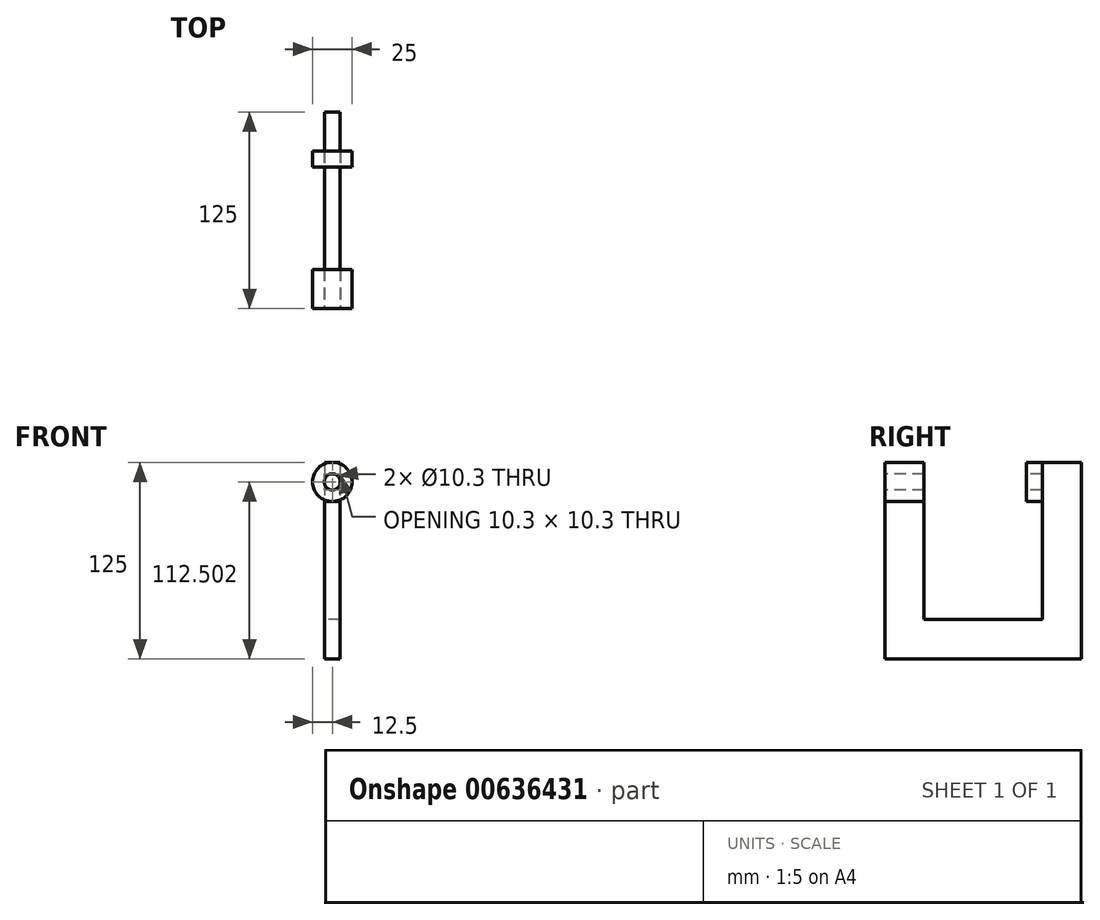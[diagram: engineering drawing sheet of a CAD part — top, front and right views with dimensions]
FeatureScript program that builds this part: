
annotation { "Feature Type Name" : "Feature", "Feature Type Description" : "" }
export const myFeature = defineFeature(function(context is Context, id is Id, definition is map)
    precondition{}
    {
        {
            var Q0;
            Q0=qCreatedBy(makeId("Right.planeOp"),FACE);
            var sketch = newSketch(context, id + "F0", { "sketchPlane" : qUnion([Q0])});
            skLineSegment(sketch, "E0", {"start": v(-109.86, 70.87) * mm, "end": v(-109.86, -29.13) * mm});
            skLineSegment(sketch, "E1", {"start": v(15.14, 95.87) * mm, "end": v(15.14, -29.13) * mm});
            skLineSegment(sketch, "E2", {"start": v(15.14, 95.87) * mm, "end": v(-9.86, 95.87) * mm});
            skLineSegment(sketch, "E3", {"start": v(-9.86, 95.87) * mm, "end": v(-9.86, -4.13) * mm});
            skLineSegment(sketch, "E4", {"start": v(-9.86, -4.13) * mm, "end": v(-84.86, -4.13) * mm});
            skLineSegment(sketch, "E5", {"start": v(-84.86, -4.13) * mm, "end": v(-84.86, 70.87) * mm});
            skLineSegment(sketch, "E6", {"start": v(-84.86, 70.87) * mm, "end": v(-109.86, 70.87) * mm});
            skLineSegment(sketch, "E7", {"start": v(-109.86, -29.13) * mm, "end": v(15.14, -29.13) * mm});
            skSolve(sketch);
        }
        {
            var Q0;
            Q0 = qSketchRegion(id + "F0", true);
            extrude(context, id + "F1", {"entities" : qUnion([Q0]), "endBound" : BoundingType.SYMMETRIC, "depth" : 10 * mm, "offsetDistance" : 25 * mm});
        }
        {
            var Q0;
            Q0=makeQuery(id+"F1.opExtrude","SWEPT_FACE",FACE,{"disambiguationData":[OSD([sQuery(id+"F0.wireOp",EDGE,"E3")])]});
            var sketch = newSketch(context, id + "F2", { "sketchPlane" : qUnion([Q0])});
            skCircle(sketch, "E8", {"center": v(0, 83.37) * mm, "radius": 12.5 * mm});
            skSolve(sketch);
        }
        {
            var Q0;
            Q0 = qSketchRegion(id + "F2", true);
            extrude(context, id + "F3", {"entities" : qUnion([Q0]), "depth" : 100 * mm, "offsetDistance" : 25 * mm});
        }
        {
            var Q0;
            Q0=qCreatedBy(makeId("Right.planeOp"),FACE);
            var sketch = newSketch(context, id + "F4", { "sketchPlane" : qUnion([Q0])});
            skLineSegment(sketch, "E9.bottom", {"start": v(-84.86, 0.87) * mm, "end": v(-19.86, 0.87) * mm});
            skLineSegment(sketch, "E9.top", {"start": v(-84.86, 100.87) * mm, "end": v(-19.86, 100.87) * mm});
            skLineSegment(sketch, "E9.left", {"start": v(-84.86, 0.87) * mm, "end": v(-84.86, 100.87) * mm});
            skLineSegment(sketch, "E9.right", {"start": v(-19.86, 0.87) * mm, "end": v(-19.86, 100.87) * mm});
            skSolve(sketch);
        }
        {
            var Q0;
            Q0 = qSketchRegion(id + "F4", true);
            extrude(context, id + "F5", {"entities" : qUnion([Q0]), "operationType" : NewBodyOperationType.REMOVE, "endBound" : BoundingType.SYMMETRIC, "oppositeDirection" : true, "depth" : 25 * mm, "offsetDistance" : 25 * mm});
        }
        {
            var Q0;
            Q0=makeQuery(id+"F3.opExtrude","CAP_FACE",FACE,{"disambiguationData":[OSD([sQuery(id+"F2.wireOp",EDGE,"E8")])],"isStart":false});
            var sketch = newSketch(context, id + "F6", { "sketchPlane" : qUnion([Q0])});
            skLineSegment(sketch, "E10", {"start": v(0, 83.37) * mm, "end": v(0, 95.87) * mm, "construction": true});
            skSolve(sketch);
        }
        {
            var Q0;
            Q0=sQuery(id+"F6.wireOp",VERTEX,"E10.start");
            var Q1;
            Q1=makeQuery(id+"F5.boolean.opBoolean","SPLIT",BODY,{"disambiguationData":[OD(1.0)],"derivedFrom":makeQuery(id+"F3.opExtrude","SWEPT_BODY",BODY,{"disambiguationData":[OSD([sQuery(id+"F2.wireOp",EDGE,"E8")])]})});
            hole(context, id + "F7", {"style" : HoleStyle.SIMPLE, "endStyle" : HoleEndStyle.THROUGH, "standardTappedOrClearance" : lookupTablePath({ "standard" : "ISO", "engagement" : "75%", "pitch" : "1.75 mm", "size" : "M12", "type" : "Tapped" }), "standardBlindInLast" : lookupTablePath({ "standard" : "ISO", "engagement" : "75%", "pitch" : "1.75 mm", "size" : "M12", "type" : "Tapped" }), "holeDiameter" : 10.3 * mm, "majorDiameter" : 12 * mm, "showTappedDepth" : true, "isTappedThrough" : true, "tappedDepth" : 12 * mm, "tapClearance" : 3, "locations" : qUnion([Q0]), "scope" : qUnion([Q1])});
        }
    });
